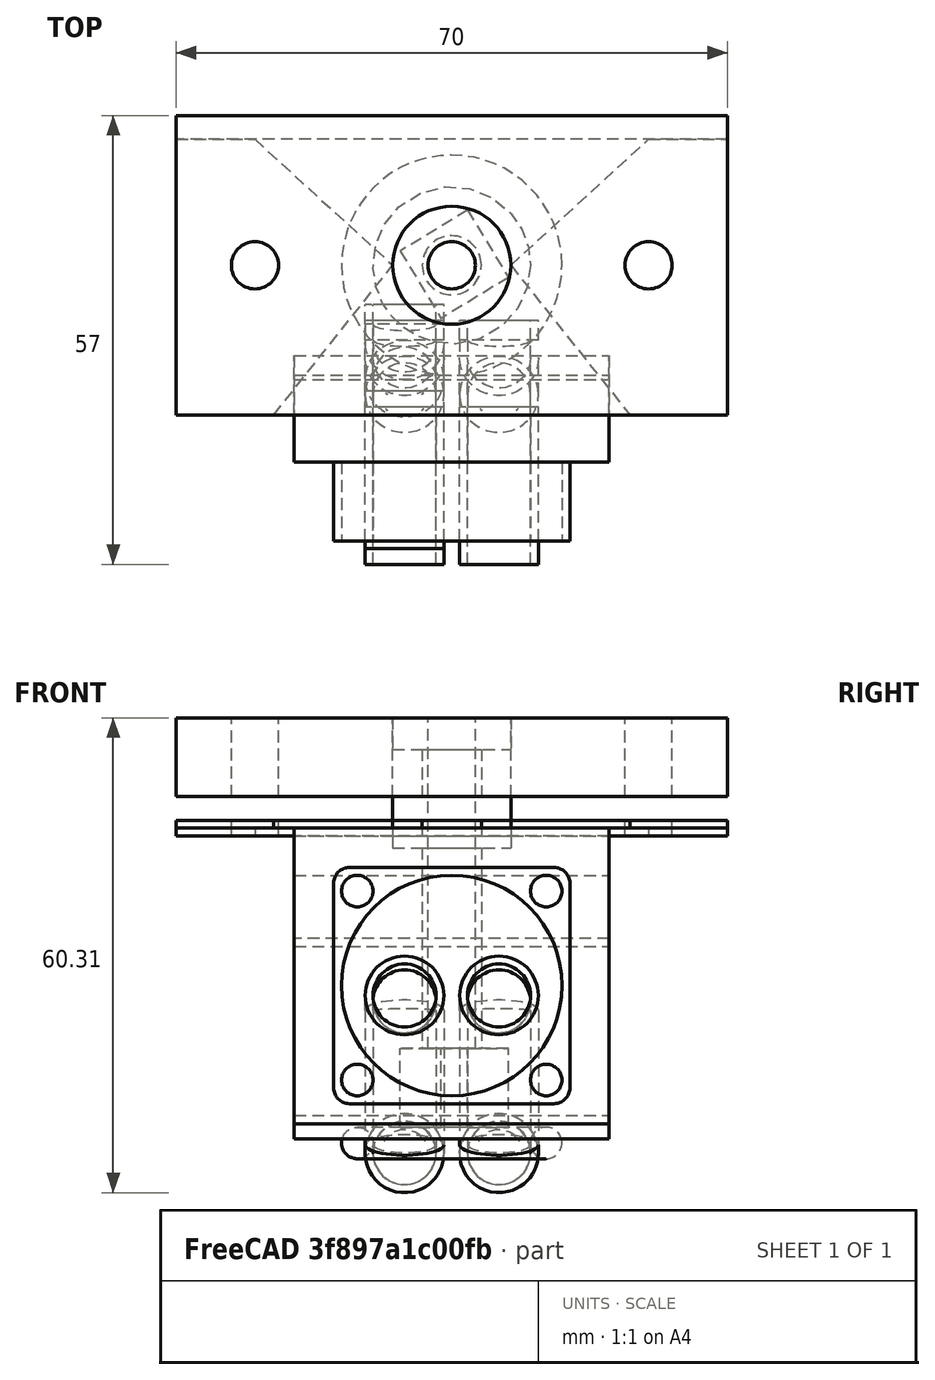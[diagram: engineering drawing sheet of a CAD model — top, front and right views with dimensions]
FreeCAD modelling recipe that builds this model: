
FCSTD DOCUMENT  (FreeCAD 0.17R13509 (Git))
Label: fan_support
License: All rights reserved
LicenseURL: http://en.wikipedia.org/wiki/All_rights_reserved
objects: Part::Cut×11, Part::Cylinder×7, Part::Extrusion×6, Part::Feature×5, Part::Part2DObjectPython×5, Part::FeaturePython×4, Part::Box×4, Part::Thickness×4, Part::MultiFuse×3, Part::Revolution×1, Part::Offset×1, Part::Torus×1, Part::Sweep×1
note: 53 computed .brp shape members not serialized (recipe doc carries the construction recipe); baked Part::Feature solids carry a one-line shape summary decoded from their .brp

FEATURE [Part::Feature] Face
  shape: bbox 7.5 x 2e-07 x 42 mm, 1 faces, 0 solids (baked)
FEATURE [Part::Revolution] Revolve
  Angle = 360
  Axis = (0,0,1)
  Base = (0,0,0)
  FaceMakerClass = Part::FaceMakerBullseye
  Solid = true
  Source = -> Face
  Symmetric = true
FEATURE [Part::Cylinder] Cylinder  label="Cilindro"
  Angle = 360
  AttacherType = Attacher::AttachEngine3D
  Height = 100
  Placement = pos=(0,0,-6) rot=(0,0,1;0rad)
  Radius = 3
FEATURE [Part::Cut] Cut  label="extruder"
  Base = -> Revolve
  Placement = pos=(0,0,-31) rot=(0,0,1;0rad)
  Tool = -> Cylinder
FEATURE [Part::Part2DObjectPython] Rectangle  # Draft 2D object (typed FeaturePython)
  ChamferSize = 0
  Columns = 1
  FilletRadius = 2
  Height = 30
  Length = 30
  MakeFace = true
  Placement = pos=(-15,-15,0) rot=(0,0,1;0rad)
  Rows = 1
FEATURE [Part::Extrusion] Extrude
  Base = -> Rectangle
  Dir = (0,0,1)
  DirMode = 2
  FaceMakerClass = Part::FaceMakerBullseye
  LengthFwd = 10
  LengthRev = 0
  Solid = true
  Symmetric = false
FEATURE [Part::Cylinder] Cylinder001  label="Cilindro001"
  Angle = 360
  AttacherType = Attacher::AttachEngine3D
  Height = 10
  Placement = pos=(12,12,0) rot=(0,0,1;0rad)
  Radius = 2
FEATURE [Part::FeaturePython] Array  # Draft array (typed FeaturePython)
  Angle = 360
  ArrayType = 0
  Axis = (0,0,1)
  Base = -> Cylinder001
  Center = (0,0,0)
  Fuse = false
  IntervalAxis = (0,0,0)
  IntervalX = (-24,0,0)
  IntervalY = (0,-24,0)
  IntervalZ = (0,0,0)
  NumberPolar = 1
  NumberX = 2
  NumberY = 2
  NumberZ = 1
FEATURE [Part::Cut] Cut001
  Base = -> Extrude
  Tool = -> Array
FEATURE [Part::Cylinder] Cylinder002  label="Cilindro002"
  Angle = 360
  AttacherType = Attacher::AttachEngine3D
  Height = 10
  Radius = 14
FEATURE [Part::Cut] Cut002  label="fan_1"
  Base = -> Cut001
  Placement = pos=(0,-25,-23) rot=(1,0,0;1.5708rad)
  Tool = -> Cylinder002
FEATURE [Part::Part2DObjectPython] Rectangle001  # Draft 2D object (typed FeaturePython)
  ChamferSize = 0
  Columns = 1
  FilletRadius = 0
  Height = 38
  Length = 70
  MakeFace = true
  Placement = pos=(-35,-24,0) rot=(0,0,1;0rad)
  Rows = 1
FEATURE [Part::Extrusion] Extrude001
  Base = -> Rectangle001
  Dir = (0,0,1)
  DirMode = 2
  FaceMakerClass = Part::FaceMakerBullseye
  LengthFwd = 10
  LengthRev = 0
  Solid = true
  Symmetric = false
FEATURE [Part::Cylinder] Cylinder003  label="Cilindro003"
  Angle = 360
  AttacherType = Attacher::AttachEngine3D
  Height = 10
  Placement = pos=(25,-5,0) rot=(0,0,1;0rad)
  Radius = 3
FEATURE [Part::FeaturePython] Array001  # Draft array (typed FeaturePython)
  Angle = 360
  ArrayType = 0
  Axis = (0,0,1)
  Base = -> Cylinder003
  Center = (0,0,0)
  Fuse = false
  IntervalAxis = (0,0,0)
  IntervalX = (-50,0,0)
  IntervalY = (0,1,0)
  IntervalZ = (0,0,0)
  NumberPolar = 1
  NumberX = 2
  NumberY = 1
  NumberZ = 1
FEATURE [Part::Cylinder] Cylinder004  label="Cilindro004"
  Angle = 360
  AttacherType = Attacher::AttachEngine3D
  Height = 10
  Placement = pos=(0,-5,0) rot=(0,0,1;0rad)
  Radius = 7.5
FEATURE [Part::MultiFuse] Fusion
  Shapes = -> [Array001,Cylinder004]
FEATURE [Part::Cut] Cut003  label="x_carr"
  Base = -> Extrude001
  Placement = pos=(0,5,1) rot=(0,0,1;0rad)
  Tool = -> Fusion
FEATURE [Part::Feature] Face001001
  shape: bbox 70 x 38 x 2e-07 mm, 0 faces, 0 solids (baked)
FEATURE [Part::Extrusion] Extrude002
  Base = -> Face001001
  Dir = (0,0,-1)
  DirMode = 2
  FaceMakerClass = Part::FaceMakerBullseye
  LengthFwd = 1
  LengthRev = 0
  Placement = pos=(0,0,1) rot=(0,0,1;0rad)
  Solid = true
  Symmetric = false
FEATURE [Part::Feature] Wire
  shape: bbox 70 x 38 x 2e-07 mm, 0 faces, 0 solids (baked)
FEATURE [Part::Extrusion] Extrude003
  Base = -> Wire
  Dir = (0,0,-1)
  DirMode = 2
  FaceMakerClass = Part::FaceMakerBullseye
  LengthFwd = 1
  LengthRev = 0
  Solid = true
  Symmetric = false
FEATURE [Part::FeaturePython] Array002  # Draft array (typed FeaturePython)
  Angle = 360
  ArrayType = 0
  Axis = (0,0,1)
  Base = -> Cylinder003
  Center = (0,0,0)
  Fuse = false
  IntervalAxis = (0,0,0)
  IntervalX = (-50,0,0)
  IntervalY = (0,1,0)
  IntervalZ = (0,0,0)
  NumberPolar = 1
  NumberX = 2
  NumberY = 1
  NumberZ = 1
  Placement = pos=(0,5,-3) rot=(0,0,1;0rad)
FEATURE [Part::FeaturePython] Array003  # Draft array (typed FeaturePython)
  Angle = 360
  ArrayType = 0
  Axis = (0,0,1)
  Base = -> Cylinder003
  Center = (0,0,0)
  Fuse = false
  IntervalAxis = (0,0,0)
  IntervalX = (-50,0,0)
  IntervalY = (0,1,0)
  IntervalZ = (0,0,0)
  NumberPolar = 1
  NumberX = 2
  NumberY = 1
  NumberZ = 1
  Placement = pos=(0,5,-3) rot=(0,0,1;0rad)
FEATURE [Part::Cut] Cut004
  Base = -> Extrude002
  Tool = -> Array003
FEATURE [Part::Cut] Cut005
  Base = -> Extrude003
  Tool = -> Array002
FEATURE [Part::Box] Box  label="Cubo"
  AttacherType = Attacher::AttachEngine3D
  Height = 10
  Length = 100
  Placement = pos=(-50,-29,-2) rot=(0,0,1;0rad)
  Width = 10
FEATURE [Part::Box] Box001  label="Cubo001"
  AttacherType = Attacher::AttachEngine3D
  Height = 10
  Length = 100
  Placement = pos=(-50,-29,-2) rot=(0,0,1;0rad)
  Width = 10
FEATURE [Part::Cut] Cut006  label="supp_a_1"
  Base = -> Cut004
  Placement = pos=(0,0,-3) rot=(0,0,1;0rad)
  Tool = -> Box
FEATURE [Part::Box] Box002  label="Cubo002"
  AttacherType = Attacher::AttachEngine3D
  Height = 10
  Length = 10
  Placement = pos=(2,7,-41) rot=(0,0,1;3.68881rad)
  Width = 10
FEATURE [Part::MultiFuse] Fusion001  label="extrusor"
  Shapes = -> [Cut,Box002]
FEATURE [Part::Feature] Wire001
  shape: bbox 2e-07 x 13.5 x 39.5 mm, 0 faces, 0 solids (baked)
FEATURE [Part::Extrusion] Extrude004
  Base = -> Wire001
  Dir = (1,0,0)
  DirMode = 2
  FaceMakerClass = Part::FaceMakerBullseye
  LengthFwd = 40
  LengthRev = 0
  Placement = pos=(-5,0,0) rot=(0,0,1;0rad)
  Solid = true
  Symmetric = false
FEATURE [Part::Cut] Cut007  label="supp_a_2"
  Base = -> Cut005
  Placement = pos=(0,0,-3) rot=(0,0,1;0rad)
  Tool = -> Box001
FEATURE [Part::Feature] Wire002
  shape: bbox 2e-07 x 13.5 x 39.5 mm, 0 faces, 0 solids (baked)
FEATURE [Part::Part2DObjectPython] DWire  # Draft 2D object (typed FeaturePython)
  ChamferSize = 0
  Closed = true
  End = (-15,-19,-4)
  FilletRadius = 0
  Length = 106.501
  MakeFace = true
  Points = (11) [(-15,-19,-3),(-15,-25,-3),(-15,-25,-40.6031),(-15,-19,-40.6031),(-15,-14.5,-42.5),(-15,-11.5,-39.5),(-15,-19,-18),(-15,-18.976,-9.02251),+3 more]
  Start = (-15,-19,-3)
  Subdivisions = 0
FEATURE [Part::Offset] Offset
  Fill = false
  Intersection = false
  Join = 0
  Mode = 0
  Placement = pos=(-1,0,0) rot=(0,0,1;0rad)
  SelfIntersection = false
  Source = -> DWire
  Value = 1
FEATURE [Part::Extrusion] Extrude005
  Base = -> Offset
  Dir = (1,0,0)
  DirMode = 2
  FaceMakerClass = Part::FaceMakerBullseye
  LengthFwd = 40
  LengthRev = 0
  Placement = pos=(-5,0,0) rot=(0,0,1;0rad)
  Solid = true
  Symmetric = false
FEATURE [Part::MultiFuse] Fusion002
  Shapes = -> [Extrude005,Cut007]
FEATURE [Part::Box] Box003  label="Cubo003"
  AttacherType = Attacher::AttachEngine3D
  Height = 28
  Length = 44
  Placement = pos=(-21,-19,-45) rot=(0,0,1;0rad)
  Width = 10
FEATURE [Part::Cut] Cut008
  Base = -> Fusion002
  Tool = -> Box003
FEATURE [Part::Torus] Torus001  label="Toro001"
  Angle1 = -180
  Angle2 = 180
  Angle3 = 360
  AttacherType = Attacher::AttachEngine3D
  Placement = pos=(0,0,-43) rot=(0,0,1;0rad)
  Radius1 = 12
  Radius2 = 2
FEATURE [Part::Part2DObjectPython] DWire001  # Draft 2D object (typed FeaturePython)
  ChamferSize = 0
  Closed = false
  End = (-20,-7.44581,-44.2636)
  FilletRadius = 2
  Length = 45.3667
  MakeFace = true
  Points = (4) [(-20,-38.4458,-24.2636),(-20,-16.9274,-24.2636),(-20,-11.4458,-44.2636),(-20,-7.44581,-44.2636)]
  Start = (-20,-38.4458,-24.2636)
  Subdivisions = 0
  Support = -> [Cut008]
FEATURE [Part::Part2DObjectPython] Circle  # Draft 2D object (typed FeaturePython)
  FirstAngle = 0
  LastAngle = 0
  MakeFace = true
  Placement = pos=(-20,-7,-44.2636) rot=(1,0,0;1.5708rad)
  Radius = 4
FEATURE [Part::Sweep] Sweep
  Frenet = false
  Sections = -> [Circle]
  Solid = true
  Spine = -> DWire001
  Transition = 1
FEATURE [Part::Thickness] Thickness
  Faces = -> Sweep [Face6,Face7]
  Intersection = false
  Join = 0
  Mode = 0
  Placement = pos=(14,2,0) rot=(0,0,1;0rad)
  SelfIntersection = false
  Value = 1
FEATURE [Part::Thickness] Thickness001
  Faces = -> Sweep [Face6,Face7]
  Intersection = false
  Join = 0
  Mode = 0
  Placement = pos=(26,0,0) rot=(0,0,1;0rad)
  SelfIntersection = false
  Value = 1
FEATURE [Part::Thickness] Thickness002
  Faces = -> Sweep [Face6,Face7]
  Intersection = false
  Join = 0
  Mode = 0
  Placement = pos=(14,0,0) rot=(0,0,1;0rad)
  SelfIntersection = false
  Value = 1
FEATURE [Part::Thickness] Thickness003
  Faces = -> Sweep [Face6,Face7]
  Intersection = false
  Join = 0
  Mode = 0
  Placement = pos=(26,0,0) rot=(0,0,1;0rad)
  SelfIntersection = false
  Value = 1
FEATURE [Part::Cylinder] Cylinder005  label="Cilindro005"
  Angle = 360
  AttacherType = Attacher::AttachEngine3D
  Height = 20
  Placement = pos=(-6,-13,-25) rot=(1,0,0;1.5708rad)
  Radius = 4
FEATURE [Part::Cylinder] Cylinder006  label="Cilindro006"
  Angle = 360
  AttacherType = Attacher::AttachEngine3D
  Height = 20
  Placement = pos=(6,-13,-25) rot=(1,0,0;1.5708rad)
  Radius = 4
FEATURE [Part::Cut] Cut009
  Base = -> Cut008
  Tool = -> Cylinder005
FEATURE [Part::Cut] Cut010
  Base = -> Cut009
  Tool = -> Cylinder006
